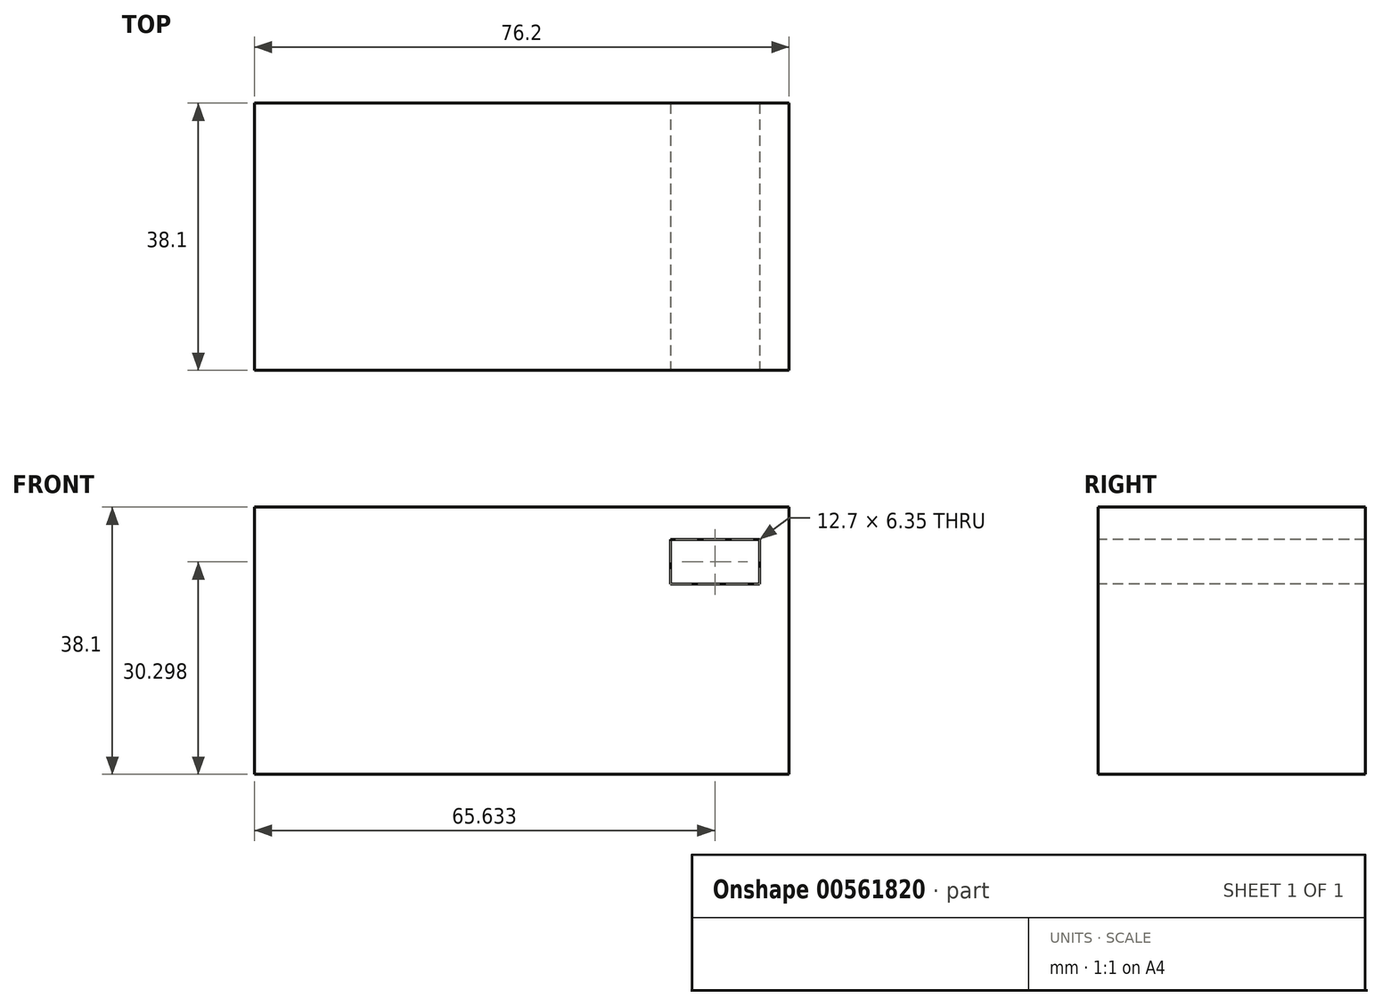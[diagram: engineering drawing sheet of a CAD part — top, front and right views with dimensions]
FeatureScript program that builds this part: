
annotation { "Feature Type Name" : "Feature", "Feature Type Description" : "" }
export const myFeature = defineFeature(function(context is Context, id is Id, definition is map)
    precondition{}
    {
        {
            var Q0;
            Q0=qCreatedBy(makeId("Front.planeOp"),FACE);
            var sketch = newSketch(context, id + "F0", { "sketchPlane" : qUnion([Q0])});
            skLineSegment(sketch, "E0.bottom", {"start": v(-38.1, 19.05) * mm, "end": v(38.1, 19.05) * mm});
            skLineSegment(sketch, "E0.top", {"start": v(-38.1, -19.05) * mm, "end": v(38.1, -19.05) * mm});
            skLineSegment(sketch, "E0.left", {"start": v(-38.1, 19.05) * mm, "end": v(-38.1, -19.05) * mm});
            skLineSegment(sketch, "E0.right", {"start": v(38.1, 19.05) * mm, "end": v(38.1, -19.05) * mm});
            skPoint(sketch, "E0.middle", {"position": v(0, 0) * mm});
            skSolve(sketch);
        }
        {
            var Q0;
            Q0 = qSketchRegion(id + "F0", true);
            extrude(context, id + "F1", {"entities" : qUnion([Q0]), "endBound" : BoundingType.SYMMETRIC, "depth" : 38.1 * mm, "offsetDistance" : 25.4 * mm});
        }
        {
            var Q0;
            Q0=qCreatedBy(makeId("Front.planeOp"),FACE);
            var sketch = newSketch(context, id + "F2", { "sketchPlane" : qUnion([Q0])});
            skLineSegment(sketch, "E1.bottom", {"start": v(33.88, 14.42) * mm, "end": v(21.18, 14.42) * mm});
            skLineSegment(sketch, "E1.top", {"start": v(33.88, 8.07) * mm, "end": v(21.18, 8.07) * mm});
            skLineSegment(sketch, "E1.left", {"start": v(33.88, 14.42) * mm, "end": v(33.88, 8.07) * mm});
            skLineSegment(sketch, "E1.right", {"start": v(21.18, 14.42) * mm, "end": v(21.18, 8.07) * mm});
            skPoint(sketch, "E1.middle", {"position": v(27.53, 11.25) * mm});
            skSolve(sketch);
        }
        {
            var Q0;
            Q0 = qSketchRegion(id + "F2", true);
            extrude(context, id + "F3", {"entities" : qUnion([Q0]), "operationType" : NewBodyOperationType.REMOVE, "endBound" : BoundingType.SYMMETRIC, "oppositeDirection" : true, "depth" : 76.2 * mm, "offsetDistance" : 25.4 * mm});
        }
    });
